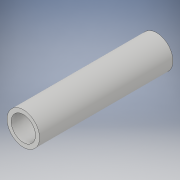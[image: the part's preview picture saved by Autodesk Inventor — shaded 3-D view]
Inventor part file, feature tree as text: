
AUTODESK INVENTOR PART (.ipt)
format: ipt  version: 2019.3 (Build 233278000, 278)  size: 95,744 bytes
history: native  units: mm
features: extrude x1, sketch x1
ambient origin geometry x8: Origin, YZ Plane, XZ Plane, XY Plane, X Axis, Y Axis, Z Axis, Center Point
bodies: Solid1 (feature_tree)
feature tree (2):
  extrude  "Extrusion1"  Depth=65.0mm
  sketch  "Sketch1"  dims[d0=15.875mm d1=2.0mm d2=65.0mm d3=0.0mm]
